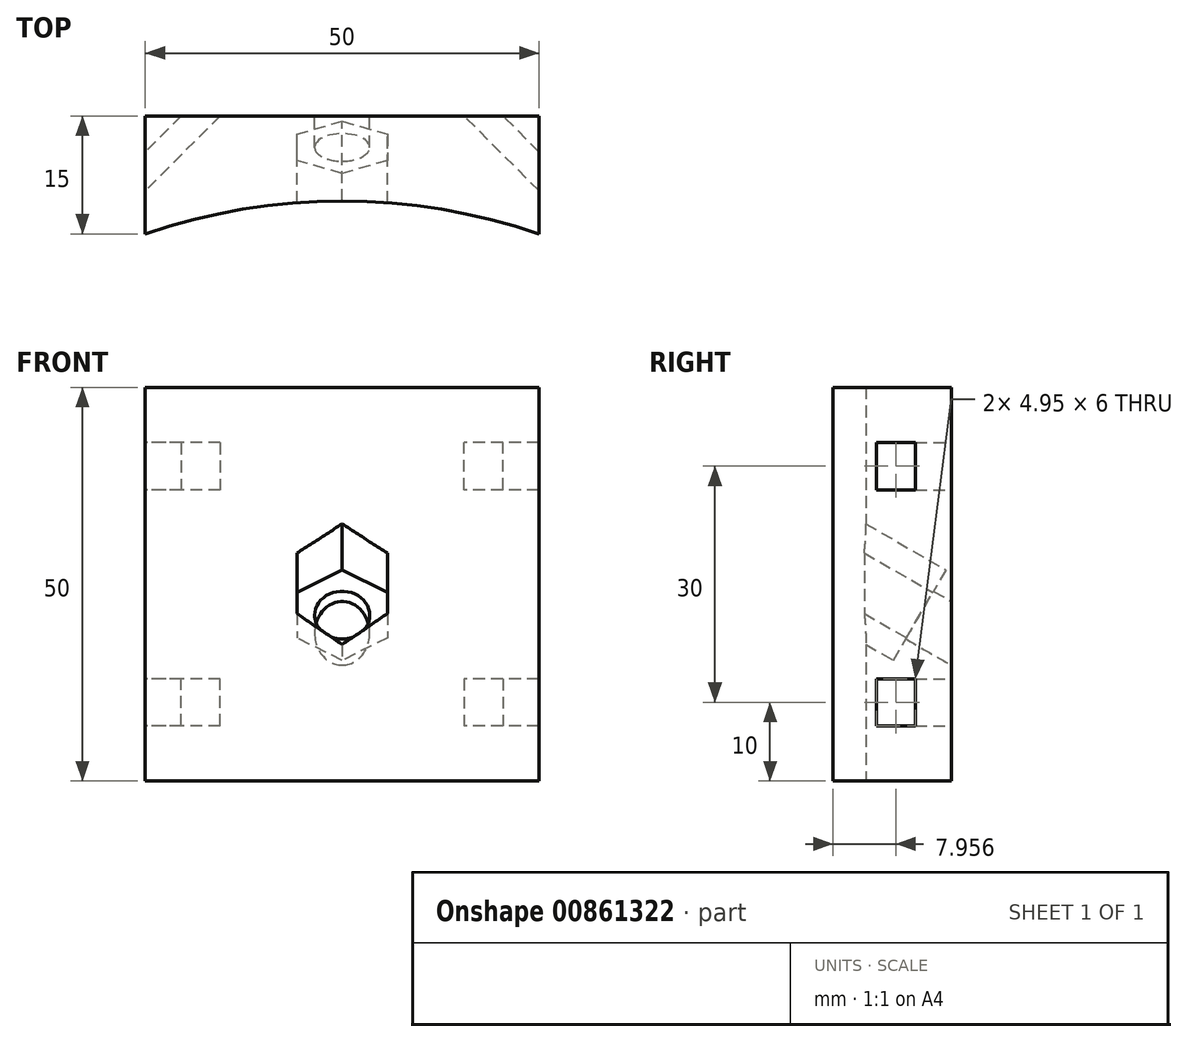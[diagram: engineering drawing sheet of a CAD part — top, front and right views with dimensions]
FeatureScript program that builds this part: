
annotation { "Feature Type Name" : "Feature", "Feature Type Description" : "" }
export const myFeature = defineFeature(function(context is Context, id is Id, definition is map)
    precondition{}
    {
        {
            var Q0;
            Q0=qCreatedBy(makeId("Top.planeOp"),FACE);
            var sketch = newSketch(context, id + "F0", { "sketchPlane" : qUnion([Q0])});
            skLineSegment(sketch, "E0.bottom", {"start": v(25, -7.5) * mm, "end": v(-25, -7.5) * mm});
            skLineSegment(sketch, "E0.top", {"start": v(25, 7.5) * mm, "end": v(-25, 7.5) * mm});
            skLineSegment(sketch, "E0.left", {"start": v(25, -7.5) * mm, "end": v(25, 7.5) * mm});
            skLineSegment(sketch, "E0.right", {"start": v(-25, -7.5) * mm, "end": v(-25, 7.5) * mm});
            skPoint(sketch, "E0.middle", {"position": v(0, 0) * mm});
            skCircle(sketch, "E1", {"center": v(0, -80.33) * mm, "radius": 77 * mm});
            skSolve(sketch);
        }
        {
            var Q0;
            Q0=makeQuery(id+"F0.imprint","IMPRINT",FACE,{"disambiguationData":[TD([[makeQuery(id+"F0.imprint","IMPRINT",EDGE,{"derivedFrom":sQuery(id+"F0.wireOp",EDGE,"E0.top")}),1.0]])]});
            extrude(context, id + "F1", {"entities" : qUnion([Q0]), "depth" : 50 * mm, "offsetDistance" : 25 * mm});
        }
        {
            var Q0;
            Q0=makeQuery(id+"F1.opExtrude","CAP_EDGE",EDGE,{"disambiguationData":[OSD([sQuery(id+"F0.wireOp",EDGE,"E0.top")])],"isStart":true});
            cPlane(context, id + "F2", {"entities" : qUnion([Q0]), "cplaneType" : CPlaneType.LINE_ANGLE, "offset" : 25 * mm, "angle" : 30 * degree, "width" : 150 * mm, "height" : 150 * mm});
        }
        {
            var Q0;
            Q0=qCreatedBy(id+"F2.planeOp",FACE);
            var sketch = newSketch(context, id + "F3", { "sketchPlane" : qUnion([Q0])});
            skCircle(sketch, "E2.cCircle", {"center": v(0, 20) * mm, "radius": 5.75 * mm, "construction": true});
            skLineSegment(sketch, "E2.0", {"start": v(-5.75, 16.68) * mm, "end": v(-5.75, 23.32) * mm});
            skLineSegment(sketch, "E2.1", {"start": v(-5.75, 23.32) * mm, "end": v(0, 26.64) * mm});
            skLineSegment(sketch, "E2.2", {"start": v(0, 26.64) * mm, "end": v(5.75, 23.32) * mm});
            skLineSegment(sketch, "E2.3", {"start": v(5.75, 23.32) * mm, "end": v(5.75, 16.68) * mm});
            skLineSegment(sketch, "E2.4", {"start": v(5.75, 16.68) * mm, "end": v(0, 13.36) * mm});
            skLineSegment(sketch, "E2.5", {"start": v(0, 13.36) * mm, "end": v(-5.75, 16.68) * mm});
            skPoint(sketch, "E2.0.midPoint", {"position": v(-5.75, 20) * mm});
            skCircle(sketch, "E3", {"center": v(0, 20) * mm, "radius": 3.5 * mm});
            skSolve(sketch);
        }
        {
            var Q0;
            Q0=makeQuery(id+"F3.imprint","IMPRINT",FACE,{"disambiguationData":[TD([[makeQuery(id+"F3.imprint","IMPRINT",EDGE,{"derivedFrom":sQuery(id+"F3.wireOp",EDGE,"E3")}),1.0]])]});
            extrude(context, id + "F4", {"entities" : qUnion([Q0]), "operationType" : NewBodyOperationType.REMOVE, "depth" : 25 * mm, "offsetDistance" : 25 * mm});
        }
        {
            var Q0;
            Q0=makeQuery(id+"F3.imprint","IMPRINT",FACE,{"disambiguationData":[TD([[makeQuery(id+"F3.imprint","IMPRINT",EDGE,{"derivedFrom":sQuery(id+"F3.wireOp",EDGE,"E2.0")}),-1.0]])]});
            var Q1;
            Q1=makeQuery(id+"F3.imprint","IMPRINT",FACE,{"disambiguationData":[TD([[makeQuery(id+"F3.imprint","IMPRINT",EDGE,{"derivedFrom":sQuery(id+"F3.wireOp",EDGE,"E3")}),1.0]])]});
            extrude(context, id + "F5", {"entities" : qUnion([Q0, Q1]), "operationType" : NewBodyOperationType.REMOVE, "depth" : 32 * mm, "offsetDistance" : 25 * mm, "hasSecondDirection" : true, "secondDirectionOppositeDirection" : false, "secondDirectionDepth" : 14 * mm});
        }
        {
            var Q0;
            Q0=makeQuery(id+"F1.opExtrude","SWEPT_EDGE",EDGE,{"disambiguationData":[OSD([sQuery(id+"F0.wireOp",EDGE,"E0.top"),sQuery(id+"F0.wireOp",EDGE,"E0.left")])]});
            cPlane(context, id + "F6", {"entities" : qUnion([Q0]), "cplaneType" : CPlaneType.LINE_ANGLE, "offset" : 25 * mm, "angle" : 45 * degree, "width" : 150 * mm, "height" : 150 * mm});
        }
        {
            var Q0;
            Q0=qCreatedBy(id+"F6.planeOp",FACE);
            var sketch = newSketch(context, id + "F7", { "sketchPlane" : qUnion([Q0])});
            skLineSegment(sketch, "E4", {"start": v(0, 0) * mm, "end": v(-18, 0) * mm, "construction": true});
            skLineSegment(sketch, "E5", {"start": v(-18, 0) * mm, "end": v(-18, 10) * mm, "construction": true});
            skLineSegment(sketch, "E6.bottom", {"start": v(-16.25, 7) * mm, "end": v(-19.75, 7) * mm});
            skLineSegment(sketch, "E6.top", {"start": v(-16.25, 13) * mm, "end": v(-19.75, 13) * mm});
            skLineSegment(sketch, "E6.left", {"start": v(-16.25, 7) * mm, "end": v(-16.25, 13) * mm});
            skLineSegment(sketch, "E6.right", {"start": v(-19.75, 7) * mm, "end": v(-19.75, 13) * mm});
            skPoint(sketch, "E6.middle", {"position": v(-18, 10) * mm});
            skLineSegment(sketch, "E7", {"start": v(0, 0) * mm, "end": v(0, 50) * mm});
            skLineSegment(sketch, "E8", {"start": v(0, 25) * mm, "end": v(-30, 25) * mm, "construction": true});
            skLineSegment(sketch, "E9.MirrorCS", {"start": v(-16.25, 37) * mm, "end": v(-19.75, 37) * mm});
            skLineSegment(sketch, "E10.MirrorCS", {"start": v(-16.25, 43) * mm, "end": v(-16.25, 37) * mm});
            skLineSegment(sketch, "E11.MirrorCS", {"start": v(-16.25, 43) * mm, "end": v(-19.75, 43) * mm});
            skLineSegment(sketch, "E12.MirrorCS", {"start": v(-19.75, 43) * mm, "end": v(-19.75, 37) * mm});
            skSolve(sketch);
        }
        {
            var Q0;
            Q0 = qSketchRegion(id + "F7", true);
            extrude(context, id + "F8", {"entities" : qUnion([Q0]), "operationType" : NewBodyOperationType.REMOVE, "endBound" : BoundingType.SYMMETRIC, "oppositeDirection" : true, "depth" : 25 * mm, "offsetDistance" : 25 * mm});
        }
        {
            var Q0;
            Q0=makeQuery(id+"F1.opExtrude","SWEPT_EDGE",EDGE,{"disambiguationData":[OSD([sQuery(id+"F0.wireOp",EDGE,"E0.top"),sQuery(id+"F0.wireOp",EDGE,"E0.right")])]});
            cPlane(context, id + "F9", {"entities" : qUnion([Q0]), "cplaneType" : CPlaneType.LINE_ANGLE, "offset" : 25 * mm, "angle" : 45 * degree, "oppositeDirection" : true, "width" : 150 * mm, "height" : 150 * mm});
        }
        {
            var Q0;
            Q0=qCreatedBy(id+"F9.planeOp",FACE);
            var sketch = newSketch(context, id + "F10", { "sketchPlane" : qUnion([Q0])});
            skLineSegment(sketch, "E13", {"start": v(0, 0) * mm, "end": v(-18, 0) * mm, "construction": true});
            skLineSegment(sketch, "E14", {"start": v(-18, 0) * mm, "end": v(-18, 10) * mm, "construction": true});
            skLineSegment(sketch, "E15", {"start": v(0, 0) * mm, "end": v(0, 50) * mm, "construction": true});
            skLineSegment(sketch, "E16", {"start": v(0, 25) * mm, "end": v(-30, 25) * mm, "construction": true});
            skLineSegment(sketch, "E17.bottom", {"start": v(-16.25, 7) * mm, "end": v(-19.75, 7) * mm});
            skLineSegment(sketch, "E17.top", {"start": v(-16.25, 13) * mm, "end": v(-19.75, 13) * mm});
            skLineSegment(sketch, "E17.left", {"start": v(-16.25, 7) * mm, "end": v(-16.25, 13) * mm});
            skLineSegment(sketch, "E17.right", {"start": v(-19.75, 7) * mm, "end": v(-19.75, 13) * mm});
            skPoint(sketch, "E17.middle", {"position": v(-18, 10) * mm});
            skLineSegment(sketch, "E18.MirrorCS", {"start": v(-16.25, 37) * mm, "end": v(-19.75, 37) * mm});
            skLineSegment(sketch, "E19.MirrorCS", {"start": v(-16.25, 43) * mm, "end": v(-16.25, 37) * mm});
            skLineSegment(sketch, "E20.MirrorCS", {"start": v(-16.25, 43) * mm, "end": v(-19.75, 43) * mm});
            skLineSegment(sketch, "E21.MirrorCS", {"start": v(-19.75, 43) * mm, "end": v(-19.75, 37) * mm});
            skSolve(sketch);
        }
        {
            var Q0;
            Q0 = qSketchRegion(id + "F10", true);
            extrude(context, id + "F11", {"entities" : qUnion([Q0]), "operationType" : NewBodyOperationType.REMOVE, "endBound" : BoundingType.SYMMETRIC, "oppositeDirection" : true, "depth" : 25 * mm, "offsetDistance" : 25 * mm});
        }
    });
